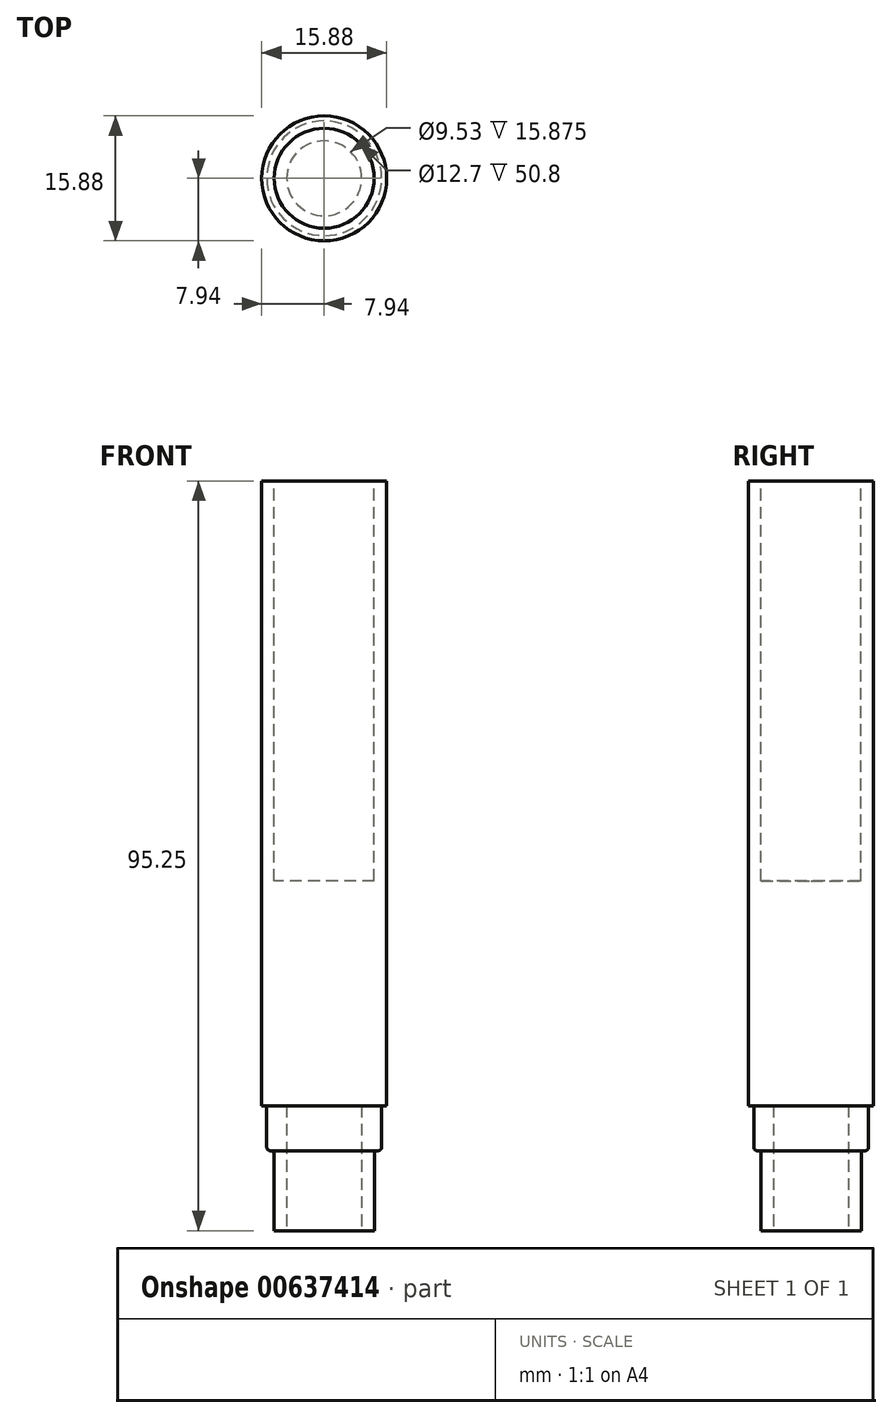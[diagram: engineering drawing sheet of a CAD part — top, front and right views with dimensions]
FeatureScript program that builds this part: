
annotation { "Feature Type Name" : "Feature", "Feature Type Description" : "" }
export const myFeature = defineFeature(function(context is Context, id is Id, definition is map)
    precondition{}
    {
        {
            var Q0;
            Q0=qCreatedBy(makeId("Top.planeOp"),FACE);
            var sketch = newSketch(context, id + "F0", { "sketchPlane" : qUnion([Q0])});
            skCircle(sketch, "E0", {"center": v(0, 0) * mm, "radius": 7.94 * mm});
            skSolve(sketch);
        }
        {
            var Q0;
            Q0=makeQuery(id+"F0.imprint","IMPRINT",FACE,{"disambiguationData":[TD([[makeQuery(id+"F0.imprint","IMPRINT",EDGE,{"derivedFrom":sQuery(id+"F0.wireOp",EDGE,"E0")}),1.0]])]});
            extrude(context, id + "F1", {"entities" : qUnion([Q0]), "depth" : 50.8 * mm, "offsetDistance" : 25.4 * mm});
        }
        {
            var Q0;
            Q0=makeQuery(id+"F1.opExtrude","CAP_FACE",FACE,{"disambiguationData":[OSD([sQuery(id+"F0.wireOp",EDGE,"E0")])],"isStart":true});
            extrude(context, id + "F2", {"entities" : qUnion([Q0]), "operationType" : NewBodyOperationType.ADD, "depth" : 28.57 * mm, "offsetDistance" : 25.4 * mm});
        }
        {
            var Q0;
            Q0=makeQuery(id+"F2.opExtrude","CAP_FACE",FACE,{"disambiguationData":[OSD([sQuery(id+"F0.wireOp",EDGE,"E0")])],"isStart":false});
            var sketch = newSketch(context, id + "F3", { "sketchPlane" : qUnion([Q0])});
            skCircle(sketch, "E1", {"center": v(0, 0) * mm, "radius": 7.3 * mm});
            skSolve(sketch);
        }
        {
            var Q0;
            Q0=makeQuery(id+"F3.imprint","IMPRINT",FACE,{"disambiguationData":[TD([[makeQuery(id+"F3.imprint","IMPRINT",EDGE,{"derivedFrom":sQuery(id+"F3.wireOp",EDGE,"E1")}),1.0]])]});
            var sketch = newSketch(context, id + "F4", { "sketchPlane" : qUnion([Q0])});
            skCircle(sketch, "E2", {"center": v(0, 0) * mm, "radius": 6.36 * mm});
            skSolve(sketch);
        }
        {
            var Q0;
            Q0=makeQuery(id+"F3.imprint","IMPRINT",FACE,{"disambiguationData":[TD([[makeQuery(id+"F3.imprint","IMPRINT",EDGE,{"derivedFrom":sQuery(id+"F3.wireOp",EDGE,"E1")}),1.0]])]});
            extrude(context, id + "F5", {"entities" : qUnion([Q0]), "operationType" : NewBodyOperationType.ADD, "depth" : 5.7 * mm, "offsetDistance" : 25.4 * mm});
        }
        {
            var Q0;
            Q0 = qSketchRegion(id + "F4", true);
            extrude(context, id + "F6", {"entities" : qUnion([Q0]), "operationType" : NewBodyOperationType.ADD, "depth" : 15.88 * mm, "offsetDistance" : 25.4 * mm});
        }
        {
            var Q0;
            Q0=makeQuery(id+"F6.boolean.opBoolean","INTERSECT",EDGE,{"derivedFrom":[makeQuery(id+"F5.opExtrude","CAP_FACE",FACE,{"disambiguationData":[OSD([sQuery(id+"F3.wireOp",EDGE,"E1")])],"isStart":false}),makeQuery(id+"F6.opExtrude","SWEPT_FACE",FACE,{"disambiguationData":[OSD([sQuery(id+"F4.wireOp",EDGE,"E2")])]})]});
            var Q1;
            Q1=makeQuery(id+"F5.opExtrude","CAP_FACE",FACE,{"disambiguationData":[OSD([sQuery(id+"F3.wireOp",EDGE,"E1")])],"isStart":false});
            fillet(context, id + "F7", {"entities" : qUnion([Q0, Q1]), "radius" : 0.43 * mm, "tangentPropagation" : true, "allowEdgeOverflow" : false});
        }
        {
            var Q0;
            Q0=makeQuery(id+"F6.opExtrude","CAP_FACE",FACE,{"disambiguationData":[OSD([sQuery(id+"F4.wireOp",EDGE,"E2")])],"isStart":false});
            var sketch = newSketch(context, id + "F8", { "sketchPlane" : qUnion([Q0])});
            skCircle(sketch, "E3", {"center": v(0, 0) * mm, "radius": 4.76 * mm});
            skSolve(sketch);
        }
        {
            var Q0;
            Q0=makeQuery(id+"F8.imprint","IMPRINT",FACE,{"disambiguationData":[TD([[makeQuery(id+"F8.imprint","IMPRINT",EDGE,{"derivedFrom":sQuery(id+"F8.wireOp",EDGE,"E3")}),1.0]])]});
            extrude(context, id + "F9", {"entities" : qUnion([Q0]), "operationType" : NewBodyOperationType.REMOVE, "oppositeDirection" : true, "depth" : 15.88 * mm, "offsetDistance" : 25.4 * mm});
        }
        {
            var Q0;
            Q0=makeQuery(id+"F1.opExtrude","CAP_FACE",FACE,{"disambiguationData":[OSD([sQuery(id+"F0.wireOp",EDGE,"E0")])],"isStart":false});
            var sketch = newSketch(context, id + "F10", { "sketchPlane" : qUnion([Q0])});
            skCircle(sketch, "E4", {"center": v(0, 0) * mm, "radius": 6.35 * mm});
            skSolve(sketch);
        }
        {
            var Q0;
            Q0 = qSketchRegion(id + "F10", true);
            extrude(context, id + "F11", {"entities" : qUnion([Q0]), "operationType" : NewBodyOperationType.REMOVE, "oppositeDirection" : true, "depth" : 50.8 * mm, "offsetDistance" : 25.4 * mm});
        }
    });
